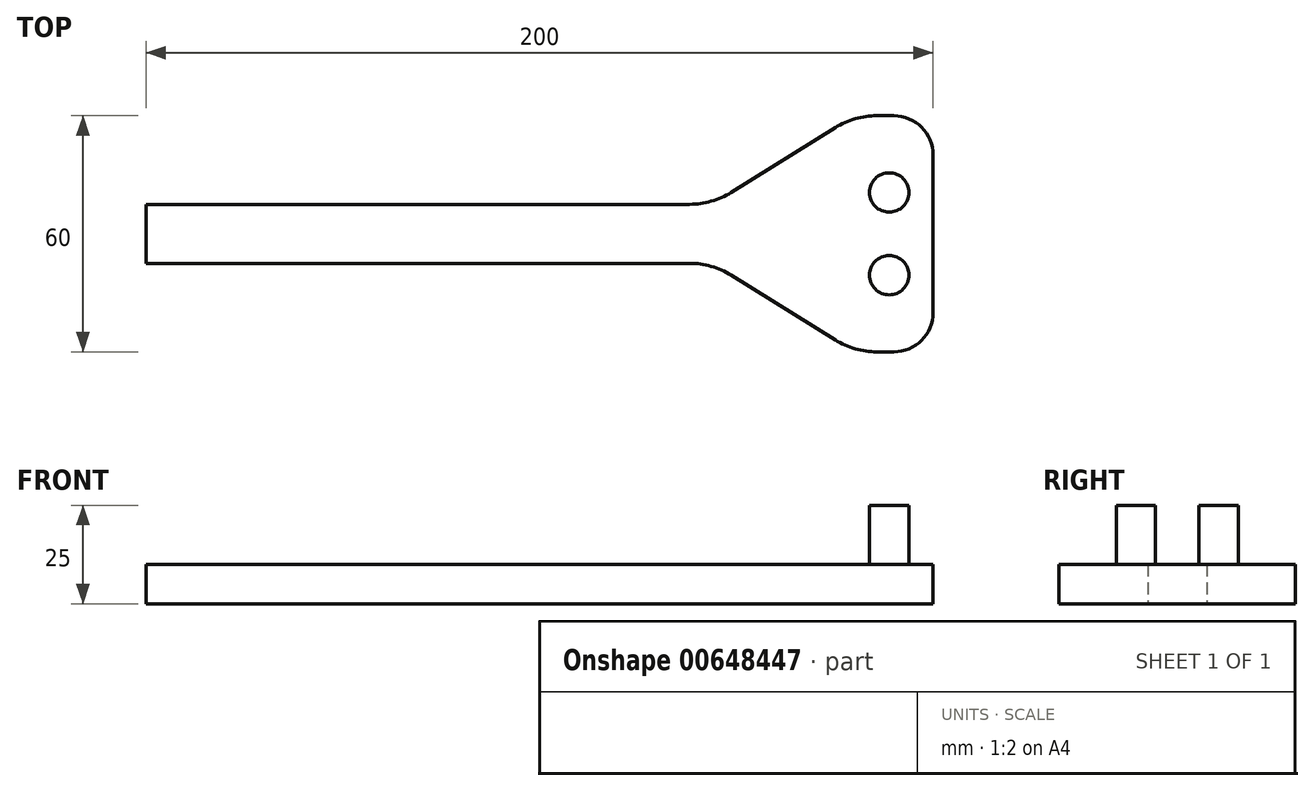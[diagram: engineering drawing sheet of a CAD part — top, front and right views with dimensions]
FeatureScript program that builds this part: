
annotation { "Feature Type Name" : "Feature", "Feature Type Description" : "" }
export const myFeature = defineFeature(function(context is Context, id is Id, definition is map)
    precondition{}
    {
        {
            var Q0;
            Q0=qCreatedBy(makeId("Top.planeOp"),FACE);
            var sketch = newSketch(context, id + "F0", { "sketchPlane" : qUnion([Q0])});
            skLineSegment(sketch, "E0.bottom", {"start": v(43.84, 7.5) * mm, "end": v(-100, 7.5) * mm});
            skLineSegment(sketch, "E0.top", {"start": v(43.84, -7.5) * mm, "end": v(-100, -7.5) * mm});
            skLineSegment(sketch, "E0.right", {"start": v(-100, 7.5) * mm, "end": v(-100, -7.5) * mm});
            skPoint(sketch, "E0.middle", {"position": v(0, 0) * mm});
            skLineSegment(sketch, "E1", {"start": v(43.84, -7.5) * mm, "end": v(80, -30) * mm});
            skLineSegment(sketch, "E2", {"start": v(80, -30) * mm, "end": v(100, -30) * mm});
            skLineSegment(sketch, "E3", {"start": v(100, -30) * mm, "end": v(100, 0) * mm});
            skLineSegment(sketch, "E4.MirrorCS", {"start": v(100, 30) * mm, "end": v(100, 0) * mm});
            skLineSegment(sketch, "E5.MirrorCS", {"start": v(80, 30) * mm, "end": v(100, 30) * mm});
            skLineSegment(sketch, "E6.MirrorCS", {"start": v(43.84, 7.5) * mm, "end": v(80, 30) * mm});
            skPoint(sketch, "E7.orphan", {"position": v(100, 7.5) * mm});
            skPoint(sketch, "E8.orphan", {"position": v(100, -7.5) * mm});
            skCircle(sketch, "E9", {"center": v(88.84, -10.5) * mm, "radius": 5 * mm});
            skCircle(sketch, "E10", {"center": v(88.84, 10.5) * mm, "radius": 5 * mm});
            skSolve(sketch);
        }
        {
            var Q0;
            Q0=makeQuery(id+"F0.imprint","IMPRINT",FACE,{"disambiguationData":[TD([[makeQuery(id+"F0.imprint","IMPRINT",EDGE,{"derivedFrom":sQuery(id+"F0.wireOp",EDGE,"E0.bottom")}),1.0]])]});
            var Q1;
            Q1=makeQuery(id+"F0.imprint","IMPRINT",FACE,{"disambiguationData":[TD([[makeQuery(id+"F0.imprint","IMPRINT",EDGE,{"derivedFrom":sQuery(id+"F0.wireOp",EDGE,"E9")}),1.0]])]});
            var Q2;
            Q2=makeQuery(id+"F0.imprint","IMPRINT",FACE,{"disambiguationData":[TD([[makeQuery(id+"F0.imprint","IMPRINT",EDGE,{"derivedFrom":sQuery(id+"F0.wireOp",EDGE,"E10")}),1.0]])]});
            extrude(context, id + "F1", {"entities" : qUnion([Q0, Q1, Q2]), "depth" : 10 * mm, "offsetDistance" : 25 * mm});
        }
        {
            var Q0;
            Q0=makeQuery(id+"F0.imprint","IMPRINT",FACE,{"disambiguationData":[TD([[makeQuery(id+"F0.imprint","IMPRINT",EDGE,{"derivedFrom":sQuery(id+"F0.wireOp",EDGE,"E9")}),1.0]])]});
            extrude(context, id + "F2", {"entities" : qUnion([Q0]), "operationType" : NewBodyOperationType.ADD, "depth" : 25 * mm, "offsetDistance" : 25 * mm});
        }
        {
            var Q0;
            Q0=makeQuery(id+"F0.imprint","IMPRINT",FACE,{"disambiguationData":[TD([[makeQuery(id+"F0.imprint","IMPRINT",EDGE,{"derivedFrom":sQuery(id+"F0.wireOp",EDGE,"E10")}),1.0]])]});
            extrude(context, id + "F3", {"entities" : qUnion([Q0]), "operationType" : NewBodyOperationType.ADD, "depth" : 25 * mm, "offsetDistance" : 25 * mm});
        }
        {
            var Q0;
            Q0=makeQuery(id+"F1.opExtrude","SWEPT_EDGE",EDGE,{"disambiguationData":[OSD([sQuery(id+"F0.wireOp",EDGE,"E4.MirrorCS"),sQuery(id+"F0.wireOp",EDGE,"E5.MirrorCS")])]});
            var Q1;
            Q1=makeQuery(id+"F1.opExtrude","SWEPT_EDGE",EDGE,{"disambiguationData":[OSD([sQuery(id+"F0.wireOp",EDGE,"E2"),sQuery(id+"F0.wireOp",EDGE,"E3")])]});
            fillet(context, id + "F4", {"entities" : qUnion([Q0, Q1]), "radius" : 10 * mm, "tangentPropagation" : true, "allowEdgeOverflow" : false});
        }
        {
            var Q0;
            Q0=makeQuery(id+"F1.opExtrude","SWEPT_EDGE",EDGE,{"disambiguationData":[OSD([sQuery(id+"F0.wireOp",EDGE,"E1"),sQuery(id+"F0.wireOp",EDGE,"E2")])]});
            var Q1;
            Q1=makeQuery(id+"F1.opExtrude","SWEPT_EDGE",EDGE,{"disambiguationData":[OSD([sQuery(id+"F0.wireOp",EDGE,"E5.MirrorCS"),sQuery(id+"F0.wireOp",EDGE,"E6.MirrorCS")])]});
            var Q2;
            Q2=makeQuery(id+"F1.opExtrude","SWEPT_EDGE",EDGE,{"disambiguationData":[OSD([sQuery(id+"F0.wireOp",EDGE,"E0.bottom"),sQuery(id+"F0.wireOp",EDGE,"E6.MirrorCS")])]});
            var Q3;
            Q3=makeQuery(id+"F1.opExtrude","SWEPT_EDGE",EDGE,{"disambiguationData":[OSD([sQuery(id+"F0.wireOp",EDGE,"E0.top"),sQuery(id+"F0.wireOp",EDGE,"E1")])]});
            fillet(context, id + "F5", {"entities" : qUnion([Q0, Q1, Q2, Q3]), "radius" : 20 * mm, "tangentPropagation" : true, "allowEdgeOverflow" : false});
        }
    });
